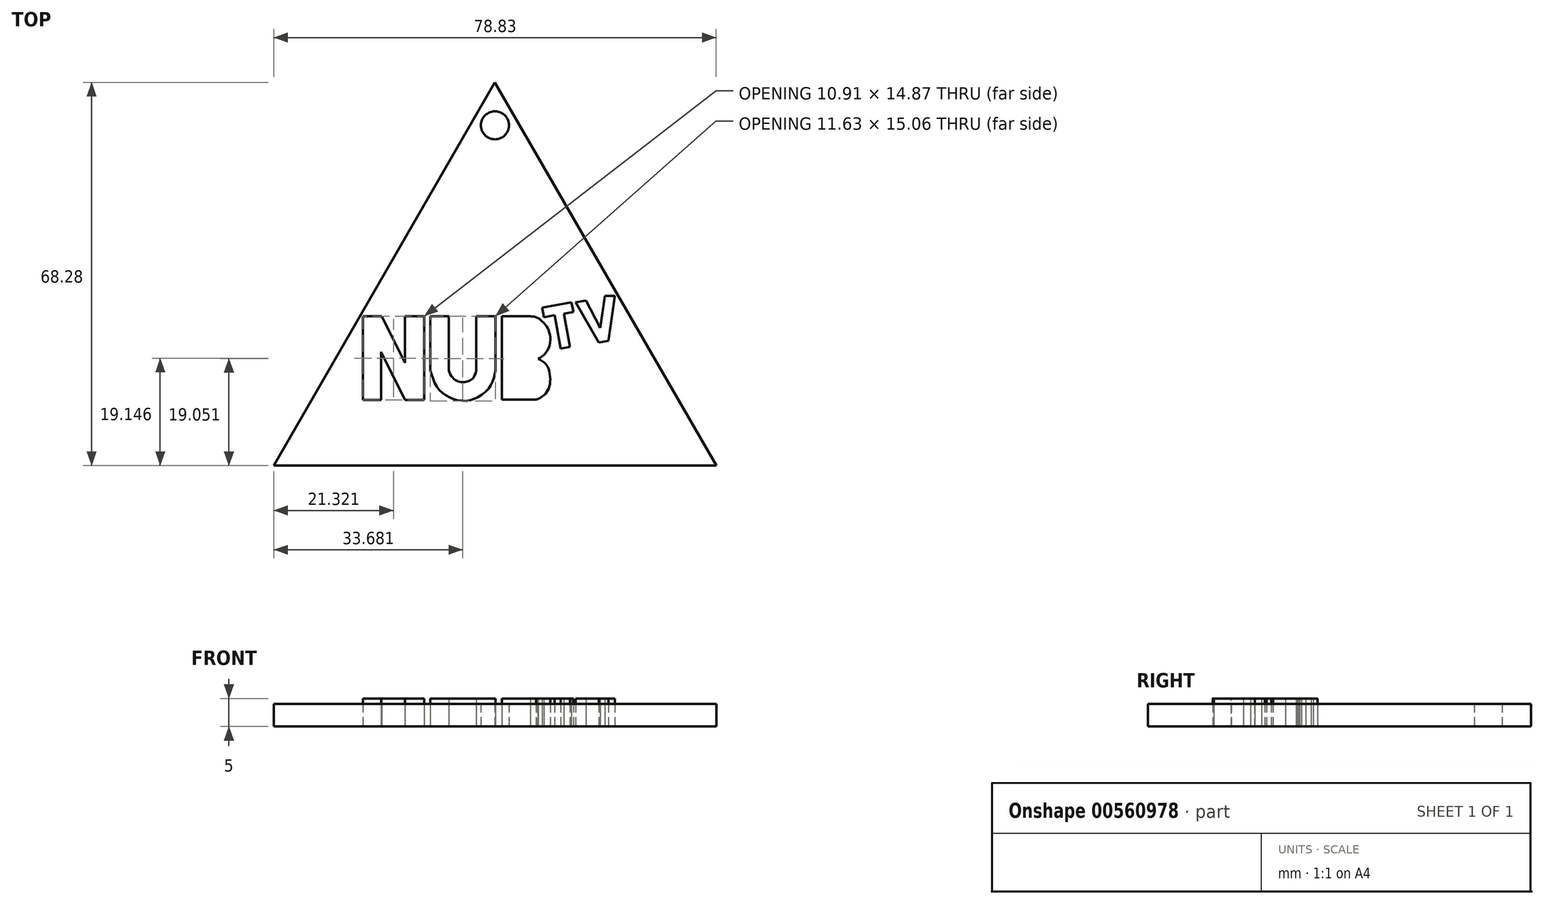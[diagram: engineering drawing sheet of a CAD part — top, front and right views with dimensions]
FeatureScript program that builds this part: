
annotation { "Feature Type Name" : "Feature", "Feature Type Description" : "" }
export const myFeature = defineFeature(function(context is Context, id is Id, definition is map)
    precondition{}
    {
        {
            var Q0;
            Q0=qCreatedBy(makeId("Top.planeOp"),FACE);
            var sketch = newSketch(context, id + "F0", { "sketchPlane" : qUnion([Q0])});
            skLineSegment(sketch, "E0", {"start": v(0.8, 36.92) * mm, "end": v(-40.23, -34.17) * mm});
            skLineSegment(sketch, "E1", {"start": v(-40.23, -34.17) * mm, "end": v(41.9, -34.17) * mm});
            skLineSegment(sketch, "E2", {"start": v(41.9, -34.17) * mm, "end": v(0.8, 36.92) * mm});
            skLineSegment(sketch, "E3", {"start": v(0.8, 35) * mm, "end": v(-38.61, -33.28) * mm});
            skLineSegment(sketch, "E4", {"start": v(-38.61, -33.28) * mm, "end": v(40.22, -33.28) * mm});
            skLineSegment(sketch, "E5", {"start": v(40.22, -33.28) * mm, "end": v(0.8, 35) * mm});
            skLineSegment(sketch, "E6", {"start": v(-22.74, -6.7) * mm, "end": v(-19.38, -6.7) * mm});
            skLineSegment(sketch, "E7", {"start": v(-19.38, -6.7) * mm, "end": v(-15.22, -15) * mm});
            skLineSegment(sketch, "E8", {"start": v(-15.22, -15) * mm, "end": v(-15.22, -6.7) * mm});
            skLineSegment(sketch, "E9", {"start": v(-15.22, -6.7) * mm, "end": v(-11.83, -6.7) * mm});
            skLineSegment(sketch, "E10", {"start": v(-11.83, -6.7) * mm, "end": v(-11.83, -21.57) * mm});
            skLineSegment(sketch, "E11", {"start": v(-11.83, -21.57) * mm, "end": v(-15.22, -21.57) * mm});
            skLineSegment(sketch, "E12", {"start": v(-15.22, -21.57) * mm, "end": v(-19.5, -13.03) * mm});
            skLineSegment(sketch, "E13", {"start": v(-19.5, -13.03) * mm, "end": v(-19.5, -21.57) * mm});
            skLineSegment(sketch, "E14", {"start": v(-19.5, -21.57) * mm, "end": v(-22.71, -21.57) * mm});
            skLineSegment(sketch, "E15", {"start": v(-22.71, -21.57) * mm, "end": v(-22.74, -6.7) * mm});
            skLineSegment(sketch, "E16", {"start": v(-10.75, -6.7) * mm, "end": v(-7.45, -6.7) * mm});
            skPoint(sketch, "E16.startSnap0", {"position": v(-13.53, -6.7) * mm});
            skLineSegment(sketch, "E17", {"start": v(-7.45, -6.7) * mm, "end": v(-7.45, -16.29) * mm});
            skFitSpline(sketch, "E18", {"points": [v(-7.45, -16.29) * mm, v(-5.71, -18.31) * mm, v(-3.77, -18.16) * mm, v(-2.52, -16.29) * mm], "startDerivative": vector(2.9, -9.2) * mm, "endDerivative": vector(2.8, 11.2) * mm});
            skLineSegment(sketch, "E19", {"start": v(-2.52, -16.29) * mm, "end": v(-2.52, -6.7) * mm});
            skLineSegment(sketch, "E20", {"start": v(-2.52, -6.7) * mm, "end": v(0.87, -6.7) * mm});
            skLineSegment(sketch, "E21", {"start": v(0.87, -6.7) * mm, "end": v(0.89, -16.29) * mm});
            skLineSegment(sketch, "E22", {"start": v(-10.75, -6.7) * mm, "end": v(-10.75, -16.29) * mm});
            skFitSpline(sketch, "E23", {"points": [v(-10.75, -16.29) * mm, v(-9.23, -19.7) * mm, v(-6.22, -21.54) * mm, v(-3, -21.46) * mm, v(0, -19.05) * mm, v(0.89, -16.29) * mm], "startDerivative": vector(5.4, -17.58) * mm, "endDerivative": vector(2.7, 15.1) * mm});
            skLineSegment(sketch, "E24", {"start": v(2.04, -6.7) * mm, "end": v(2.04, -21.53) * mm});
            skLineSegment(sketch, "E25", {"start": v(2.04, -21.53) * mm, "end": v(8.16, -21.51) * mm});
            skFitSpline(sketch, "E26", {"points": [v(8.16, -21.51) * mm, v(9.5, -20.76) * mm, v(10.28, -19.73) * mm, v(10.62, -18.44) * mm, v(10.43, -16.35) * mm, v(9.44, -14.8) * mm, v(8.46, -14.26) * mm, v(8.47, -14.26) * mm], "startDerivative": vector(7.88, 1.4) * mm, "endDerivative": vector(1.25, -0.16) * mm});
            skFitSpline(sketch, "E27", {"points": [v(8.47, -14.26) * mm, v(9.5, -13.58) * mm, v(10.47, -12.04) * mm, v(10.64, -10.3) * mm, v(10.3, -9) * mm, v(9.68, -8.06) * mm, v(8.16, -6.86) * mm, v(7.08, -6.69) * mm], "startDerivative": vector(7.86, 4.15) * mm, "endDerivative": vector(-5.2, 0.78) * mm});
            skLineSegment(sketch, "E28", {"start": v(2.04, -6.7) * mm, "end": v(7.08, -6.69) * mm});
            skLineSegment(sketch, "E29", {"start": v(43.16, -42.4) * mm, "end": v(43.16, 42.2) * mm});
            skLineSegment(sketch, "E30", {"start": v(-41.44, 42.2) * mm, "end": v(-41.44, -42.4) * mm});
            skLineSegment(sketch, "E31", {"start": v(14.44, -4.2) * mm, "end": v(9.22, -5.15) * mm});
            skLineSegment(sketch, "E32", {"start": v(9.22, -5.15) * mm, "end": v(9.53, -6.84) * mm});
            skLineSegment(sketch, "E33", {"start": v(9.53, -6.84) * mm, "end": v(11.42, -6.5) * mm});
            skLineSegment(sketch, "E34", {"start": v(11.42, -6.5) * mm, "end": v(12.52, -12.45) * mm});
            skLineSegment(sketch, "E35", {"start": v(12.52, -12.45) * mm, "end": v(14.15, -12.15) * mm});
            skLineSegment(sketch, "E36", {"start": v(14.15, -12.15) * mm, "end": v(13.05, -6.24) * mm});
            skLineSegment(sketch, "E37", {"start": v(13.05, -6.24) * mm, "end": v(14.78, -5.92) * mm});
            skLineSegment(sketch, "E38", {"start": v(14.78, -5.92) * mm, "end": v(14.44, -4.2) * mm});
            skLineSegment(sketch, "E39", {"start": v(22.17, -3.04) * mm, "end": v(21.02, -11.02) * mm});
            skLineSegment(sketch, "E40", {"start": v(21.02, -11.02) * mm, "end": v(19.3, -11.34) * mm});
            skLineSegment(sketch, "E41", {"start": v(19.3, -11.34) * mm, "end": v(15.2, -4.2) * mm});
            skLineSegment(sketch, "E42", {"start": v(15.2, -4.2) * mm, "end": v(17, -3.86) * mm});
            skLineSegment(sketch, "E43", {"start": v(17, -3.86) * mm, "end": v(19.57, -8.75) * mm});
            skLineSegment(sketch, "E44", {"start": v(19.57, -8.75) * mm, "end": v(20.4, -3.04) * mm});
            skLineSegment(sketch, "E45", {"start": v(20.4, -3.04) * mm, "end": v(22.17, -3.04) * mm});
            skLineSegment(sketch, "E46", {"start": v(-41.57, 42.2) * mm, "end": v(-41.57, -42.55) * mm});
            skLineSegment(sketch, "E47", {"start": v(-41.57, -42.55) * mm, "end": v(43.29, -42.55) * mm});
            skLineSegment(sketch, "E48", {"start": v(-41.44, 42.2) * mm, "end": v(-41.44, 42.32) * mm});
            skLineSegment(sketch, "E49", {"start": v(-41.57, 42.2) * mm, "end": v(-41.57, 42.32) * mm});
            skLineSegment(sketch, "E50", {"start": v(-41.57, 42.32) * mm, "end": v(43.16, 42.53) * mm});
            skCircle(sketch, "E51", {"center": v(0.8, 27.35) * mm, "radius": 2.5 * mm});
            skSolve(sketch);
        }
        {
            var Q0;
            Q0=makeQuery(id+"F0.imprint","IMPRINT",FACE,{"disambiguationData":[TD([[makeQuery(id+"F0.imprint","IMPRINT",EDGE,{"derivedFrom":sQuery(id+"F0.wireOp",EDGE,"E3")}),1.0]])]});
            extrude(context, id + "F1", {"entities" : qUnion([Q0]), "depth" : 4 * mm, "offsetDistance" : 25 * mm});
        }
        {
            var Q0;
            Q0=makeQuery(id+"F0.imprint","IMPRINT",FACE,{"disambiguationData":[TD([[makeQuery(id+"F0.imprint","IMPRINT",EDGE,{"derivedFrom":sQuery(id+"F0.wireOp",EDGE,"E6")}),-1.0]])]});
            var Q1;
            Q1=makeQuery(id+"F0.imprint","IMPRINT",FACE,{"disambiguationData":[TD([[makeQuery(id+"F0.imprint","IMPRINT",EDGE,{"derivedFrom":sQuery(id+"F0.wireOp",EDGE,"E16")}),-1.0]])]});
            var Q2;
            Q2=makeQuery(id+"F0.imprint","IMPRINT",FACE,{"disambiguationData":[TD([[makeQuery(id+"F0.imprint","IMPRINT",EDGE,{"derivedFrom":sQuery(id+"F0.wireOp",EDGE,"E24")}),1.0]])]});
            var Q3;
            Q3=makeQuery(id+"F0.imprint","IMPRINT",FACE,{"disambiguationData":[TD([[makeQuery(id+"F0.imprint","IMPRINT",EDGE,{"derivedFrom":sQuery(id+"F0.wireOp",EDGE,"E31")}),1.0]])]});
            var Q4;
            Q4=makeQuery(id+"F0.imprint","IMPRINT",FACE,{"disambiguationData":[TD([[makeQuery(id+"F0.imprint","IMPRINT",EDGE,{"derivedFrom":sQuery(id+"F0.wireOp",EDGE,"E39")}),-1.0]])]});
            extrude(context, id + "F2", {"entities" : qUnion([Q0, Q1, Q2, Q3, Q4]), "depth" : 5 * mm, "offsetDistance" : 25 * mm});
        }
    });
